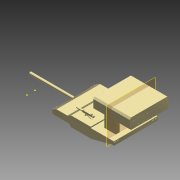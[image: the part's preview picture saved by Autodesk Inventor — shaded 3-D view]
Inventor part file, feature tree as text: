
AUTODESK INVENTOR PART (.ipt)
format: ipt  version: 2015 (Build 190159000, 159)  size: 833,536 bytes
history: native  units: in
note: dims shown in document units (in); Inventor stores cm internally (conversion verified against a paired STEP export)
features: sketch x13, extrude x8, projected_geometry x7, plane x4, hole x2, mirror x1, chamfer x1, other x1
ambient origin geometry x8: Origin, YZ Plane, XZ Plane, XY Plane, X Axis, Y Axis, Z Axis, Center Point
bodies: Solid1 (feature_tree)
feature tree (37):
  extrude  "Extrusion1"  Depth=3.0in
  extrude  "Extrusion2"  [1 undecoded]
  sketch  "Sketch4"  dims[d19=0.36in d20=0.75in d21=0.375in d22=0.25in d23=0.5635in d24=0.365in d25=0.0in d26=-0.5625in]
  sketch  "Sketch5"  dims[d27=0.1in d28=90.0deg]
  hole  "Hole2"  [1 undecoded]
  plane  "Work Plane2"
  extrude  "Extrusion3"  [1 undecoded]
  plane  "Work Plane3"
  mirror  "Mirror1"
  sketch  "Sketch9"  dims[d34=0.4775in d35=0.477in]
  sketch  "Sketch10"  dims[d36=0.2673in d37=0.267in d38=1.0in d39=0.0in]
  extrude  "Extrusion4"  Depth=0.477in
  plane  "Work Plane4"
  extrude  "Extrusion5"  Depth=0.267in
  chamfer  "Chamfer1"  Distance=1.0in
  extrude  "Extrusion6"  Depth=2.5in
  extrude  "Extrusion7"  Depth=0.336in
  extrude  "Extrusion8"  Depth=0.336in
  hole  "Hole3"  [1 undecoded]
  sketch  "Sketch1"  dims[d2=3.0in d3=0.0in d5=1.5in]
  other  "Image1"
  sketch  "Sketch2"  dims[d6=3.0in d7=0.0in]
  projected_geometry  "Projected Loop3"
  projected_geometry  "Projected Loop4"
  plane  "Work Plane1"
  sketch  "Sketch7"  dims[d29=0.1in d30=0.0in d31=-0.875in]
  sketch  "Sketch11"  dims[d42=2.5in d43=0.3364in]
  sketch  "Sketch12"  dims[d44=0.336in d45=0.336in]
  sketch  "Sketch13"  dims[d46=0.336in d47=0.336in]
  sketch  "Sketch14"  dims[d48=0.336in d49=0.336in]
  projected_geometry  "Projected Loop5"
  sketch  "Sketch15"  dims[d50=0.336in]
  projected_geometry  "Projected Loop6"
  projected_geometry  "Projected Loop7"
  projected_geometry  "Projected Loop8"
  sketch  "Sketch16"  dims[d51=0.168in d52=0.185in d54=2.5in d55=0.0in d56=0.1in d57=0.125in d58=45.0deg d59=0.001in d60=0.0in d61=0.4in d62=0.4in d63=0.2in d64=0.2in d65=0.03in d66=0.0in d67=0.4in d68=0.4in d69=0.165in d70=0.165in d71=0.165in d72=0.03in d73=0.0in d74=0.15in d75=0.75in d76=0.119in d77=0.25in d78=0.5635in d79=3.8in d80=0.0in]
  projected_geometry  "Projected Loop9"
note: 4 required parameter values undecoded (feature->parameter linkage not recoverable at this tier; creation-order binding heuristic only, values carry confidence <= 0.55)
